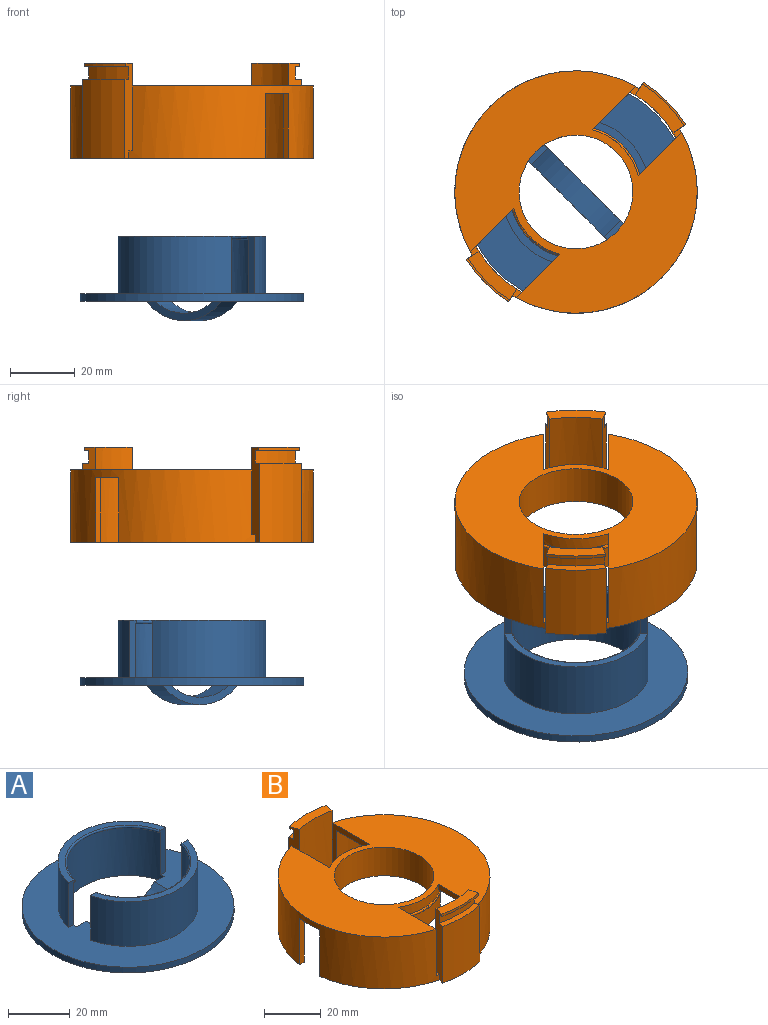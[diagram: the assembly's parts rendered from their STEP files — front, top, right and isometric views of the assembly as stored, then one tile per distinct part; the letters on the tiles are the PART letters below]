
ASSEMBLY  parts=2 mates=1
PART A: 19 faces, bbox 68.8x68.8x26 mm
  f0: torus R=20.4mm, axis (0,0,-1), area 83.2mm2, adj f2,f10,f11,f13
  f1: cylinder r=20.4mm len=40.2mm, axis (0,0,-1), area 1032.8mm2, adj f3,f5,f6,f7,f14,f18
  f2: cylinder r=20.4mm len=40.2mm, axis (0,0,-1), area 1032.8mm2, adj f0,f3,f5,f10,f11,f15
  f3: plane 68.8x68.8mm, normal (0,0,1), area 2209.7mm2, adj f1,f2,f4,f6,f7,f8,f10,f11
  f4: cylinder r=34.4mm len=68.8mm, axis (0,0,-1), area 497.1mm2, adj f3,f5
  f5: plane 68.8x68.8mm, normal (0,0,-1), area 2462.8mm2, adj f1,f2,f4,f14,f15,f16
  f6: plane 17.7x2.88mm, normal (0,-1,0), area 42.3mm2, adj f1,f3,f8,f9,f18
  f7: plane 17.7x2.88mm, normal (0,-1,0), area 42.3mm2, adj f1,f3,f8,f9,f18
  f8: cylinder r=22.7mm len=44.29mm, axis (0,0,-1), area 1083.8mm2, adj f3,f6,f7,f9
  f9: plane 44.29x17.7mm, normal (0,0,1), area 132.5mm2, adj f6,f7,f8,f18
  f10: plane 17.7x2.88mm, normal (0,1,0), area 42.3mm2, adj f0,f2,f3,f12,f13
  f11: plane 17.7x2.88mm, normal (0,1,0), area 42.3mm2, adj f0,f2,f3,f12,f13
  f12: cylinder r=22.7mm len=44.29mm, axis (0,0,-1), area 1083.8mm2, adj f3,f10,f11,f13
  f13: plane 44.29x17.7mm, normal (0,0,1), area 132.5mm2, adj f0,f10,f11,f12
  f14: plane 40.2x8.26mm, normal (0,1,0), area 99mm2, adj f1,f3,f5,f16,f17
  f15: plane 40.2x8.26mm, normal (0,-1,0), area 99mm2, adj f2,f3,f5,f16,f17
  f16: cylinder r=25.96mm len=33.09mm, axis (0,-1,0), area 251.2mm2, adj f5,f14,f15
  f17: cylinder r=23.66mm len=31.39mm, axis (0,-1,0), area 240.3mm2, adj f3,f14,f15
  f18: torus R=20.4mm, axis (0,0,-1), area 83.2mm2, adj f1,f6,f7,f9
PART B: 42 faces, bbox 74.6x79.2x29.3 mm
  f0: cylinder r=37.3mm len=72.54mm, axis (0,0,-1), area 1967.2mm2, adj f1,f3,f5,f8,f13,f14,f15,f18
  f1: plane 2.73x1.83mm, normal (0,0,1), area 3.7mm2, adj f0,f4,f22,f35
  f2: cylinder r=37.3mm len=72.54mm, axis (0,0,-1), area 1967.2mm2, adj f5,f6,f12,f14,f16,f18,f20,f23
  f3: plane 2.73x1.83mm, normal (0,0,1), area 3.7mm2, adj f0,f17,f21,f27
  f4: cylinder r=35mm len=69.28mm, axis (0,0,1), area 2084.7mm2, adj f1,f6,f8,f12,f13,f14,f22,f23
  f5: plane 74.6x71.87mm, normal (0,0,1), area 2691.7mm2, adj f0,f2,f7,f9,f20,f21,f22,f23
  f6: plane 67.08x27.3mm, normal (0,0,-1), area 1019.6mm2, adj f2,f4,f7,f12,f16,f17,f20,f23
  f7: cylinder r=19.8mm len=39.6mm, axis (0,0,1), area 298.6mm2, adj f5,f6,f8,f19,f20,f21,f22,f23
  f8: plane 67.08x27.3mm, normal (0,0,-1), area 1019.6mm2, adj f0,f4,f7,f13,f15,f17,f21,f22
  f9: cylinder r=17.5mm len=35mm, axis (0,0,-1), area 1352.5mm2, adj f5,f11
  f10: cylinder r=19.8mm len=39.6mm, axis (0,0,1), area 917.5mm2, adj f11,f19
  f11: plane 39.6x39.6mm, normal (0,0,-1), area 269.5mm2, adj f9,f10
  f12: plane 20x2.32mm, normal (0,-1,0), area 46.4mm2, adj f2,f4,f6,f14
  f13: plane 20x2.32mm, normal (0,-1,0), area 46.4mm2, adj f0,f4,f8,f14
  f14: plane 73.93x34.6mm, normal (0,0,-1), area 279.8mm2, adj f0,f2,f4,f12,f13,f34,f35,f36
  f15: plane 20x2.32mm, normal (0,1,0), area 46.4mm2, adj f0,f8,f17,f18
  f16: plane 20x2.32mm, normal (0,1,0), area 46.4mm2, adj f2,f6,f17,f18
  f17: cylinder r=35mm len=69.28mm, axis (0,0,1), area 2084.7mm2, adj f3,f6,f8,f15,f16,f18,f20,f21
  f18: plane 73.93x34.6mm, normal (0,0,-1), area 279.8mm2, adj f0,f2,f15,f16,f17,f26,f27,f28
  f19: torus R=19.8mm, axis (0,0,1), area 198.6mm2, adj f7,f10
  f20: plane 20x18.85mm, normal (-1,0,0), area 85.7mm2, adj f2,f5,f6,f7,f17,f24
  f21: plane 20x18.85mm, normal (1,0,0), area 85.7mm2, adj f0,f3,f5,f7,f8,f17
  f22: plane 20x18.85mm, normal (1,0,0), area 85.7mm2, adj f0,f1,f4,f5,f7,f8
  f23: plane 20x18.85mm, normal (-1,0,0), area 85.7mm2, adj f2,f4,f5,f6,f7,f25
  f24: plane 2.73x1.83mm, normal (0,0,1), area 3.7mm2, adj f2,f17,f20,f26
  f25: plane 2.73x1.83mm, normal (0,0,1), area 3.7mm2, adj f2,f4,f23,f34
  f26: plane 29.3x4.47mm, normal (0.97,0.23,0), area 119.8mm2, adj f2,f17,f18,f24,f28,f29,f30,f31
  f27: plane 29.3x4.47mm, normal (-0.97,0.23,0), area 119.8mm2, adj f0,f3,f17,f18,f28,f29,f30,f31
  f28: cylinder r=39.6mm len=24.4mm, axis (0,0,1), area 455.3mm2, adj f18,f26,f27,f33
  f29: plane 18.17x4.89mm, normal (0,0,1), area 68.4mm2, adj f17,f26,f27,f30
  f30: cylinder r=38.93mm len=18.17mm, axis (0,0,1), area 18.3mm2, adj f26,f27,f29,f31
  f31: plane 18.17x2.66mm, normal (0,0,-1), area 29.2mm2, adj f26,f27,f30,f32
  f32: cylinder r=37.3mm len=17.42mm, axis (0,0,1), area 68.6mm2, adj f26,f27,f31,f33
  f33: plane 18.49x3.33mm, normal (0,0,1), area 41.7mm2, adj f26,f27,f28,f32
  f34: plane 29.3x4.47mm, normal (0.97,-0.23,0), area 119.8mm2, adj f2,f4,f14,f25,f36,f37,f38,f39
  f35: plane 29.3x4.47mm, normal (-0.97,-0.23,0), area 119.8mm2, adj f0,f1,f4,f14,f36,f37,f38,f39
  f36: cylinder r=39.6mm len=24.4mm, axis (0,0,1), area 455.3mm2, adj f14,f34,f35,f37
  f37: plane 18.49x3.33mm, normal (0,0,1), area 41.7mm2, adj f34,f35,f36,f38
  f38: cylinder r=37.3mm len=17.42mm, axis (0,0,1), area 68.6mm2, adj f34,f35,f37,f39
  f39: plane 18.17x2.66mm, normal (0,0,-1), area 29.2mm2, adj f34,f35,f38,f40
  f40: cylinder r=38.93mm len=18.17mm, axis (0,0,1), area 18.3mm2, adj f34,f35,f39,f41
  f41: plane 18.17x4.89mm, normal (0,0,1), area 68.4mm2, adj f4,f34,f35,f40
PLACE A rot(axis=(0,0,-1),45deg) t=(-20.03,-18.14,-52.17)mm
PLACE B rot(axis=(0,0,-1),45deg) t=(-20.03,-18.14,-8.19)mm
MATE slider A.f4 <-> B.f17  axis (0,0,-1) through (-20.03,-18.14,-72.17)mm
